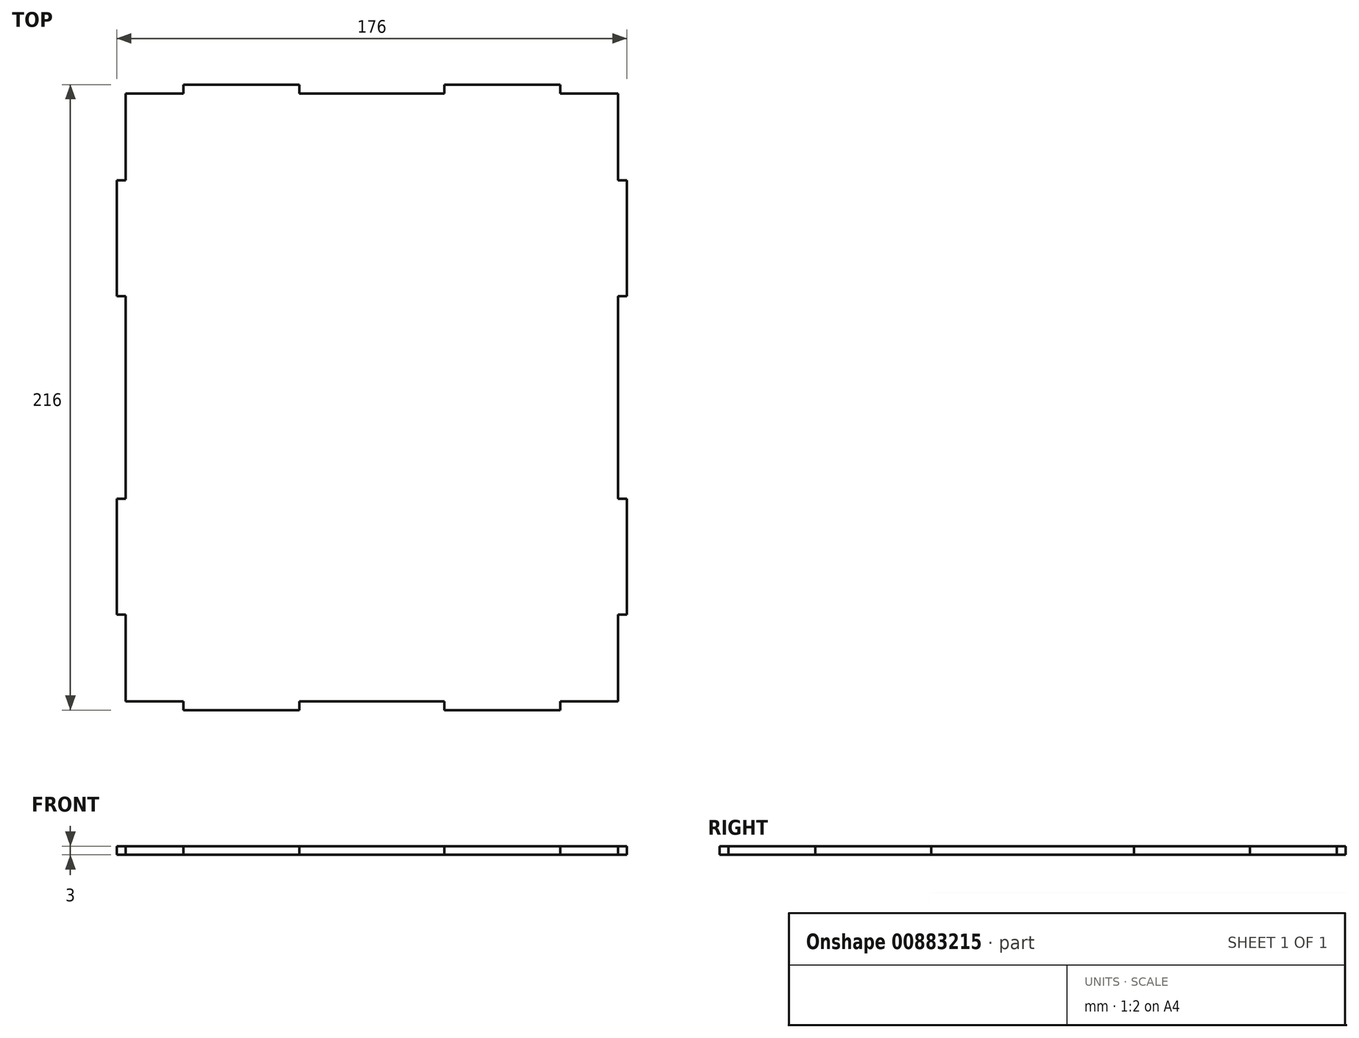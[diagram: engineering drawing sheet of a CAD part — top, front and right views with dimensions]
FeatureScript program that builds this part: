
annotation { "Feature Type Name" : "Feature", "Feature Type Description" : "" }
export const myFeature = defineFeature(function(context is Context, id is Id, definition is map)
    precondition{}
    {
        {
            var Q0;
            Q0=qCreatedBy(makeId("Top.planeOp"),FACE);
            var sketch = newSketch(context, id + "F0", { "sketchPlane" : qUnion([Q0])});
            skLineSegment(sketch, "E0.bottom", {"start": v(85, 105) * mm, "end": v(-85, 105) * mm});
            skLineSegment(sketch, "E0.top", {"start": v(85, -105) * mm, "end": v(-85, -105) * mm});
            skLineSegment(sketch, "E0.left", {"start": v(85, 105) * mm, "end": v(85, -105) * mm});
            skLineSegment(sketch, "E0.right", {"start": v(-85, 105) * mm, "end": v(-85, -105) * mm});
            skPoint(sketch, "E0.middle", {"position": v(0, 0) * mm});
            skLineSegment(sketch, "E1", {"start": v(85, 75) * mm, "end": v(88, 75) * mm});
            skLineSegment(sketch, "E2", {"start": v(88, 75) * mm, "end": v(88, 35) * mm});
            skLineSegment(sketch, "E3", {"start": v(88, 35) * mm, "end": v(85, 35) * mm});
            skLineSegment(sketch, "E4", {"start": v(25, 105) * mm, "end": v(25, 108) * mm});
            skLineSegment(sketch, "E5", {"start": v(25, 108) * mm, "end": v(65, 108) * mm});
            skLineSegment(sketch, "E6", {"start": v(65, 108) * mm, "end": v(65, 105) * mm});
            skLineSegment(sketch, "E7.MirrorCS", {"start": v(65, -108) * mm, "end": v(65, -105) * mm});
            skLineSegment(sketch, "E8.MirrorCS", {"start": v(25, -108) * mm, "end": v(65, -108) * mm});
            skLineSegment(sketch, "E9.MirrorCS", {"start": v(25, -105) * mm, "end": v(25, -108) * mm});
            skLineSegment(sketch, "E10.MirrorCS", {"start": v(-88, 35) * mm, "end": v(-85, 35) * mm});
            skLineSegment(sketch, "E11.MirrorCS", {"start": v(-85, 75) * mm, "end": v(-88, 75) * mm});
            skLineSegment(sketch, "E12.MirrorCS", {"start": v(-88, 75) * mm, "end": v(-88, 35) * mm});
            skLineSegment(sketch, "E13", {"start": v(85, -75) * mm, "end": v(88, -75) * mm});
            skLineSegment(sketch, "E14", {"start": v(88, -75) * mm, "end": v(88, -35) * mm});
            skLineSegment(sketch, "E15", {"start": v(88, -35) * mm, "end": v(85, -35) * mm});
            skLineSegment(sketch, "E16.MirrorCS", {"start": v(-88, -35) * mm, "end": v(-85, -35) * mm});
            skLineSegment(sketch, "E17.MirrorCS", {"start": v(-88, -75) * mm, "end": v(-88, -35) * mm});
            skLineSegment(sketch, "E18.MirrorCS", {"start": v(-85, -75) * mm, "end": v(-88, -75) * mm});
            skLineSegment(sketch, "E19.MirrorCS", {"start": v(-25, 105) * mm, "end": v(-25, 108) * mm});
            skLineSegment(sketch, "E20.MirrorCS", {"start": v(-25, 108) * mm, "end": v(-65, 108) * mm});
            skLineSegment(sketch, "E21.MirrorCS", {"start": v(-65, 108) * mm, "end": v(-65, 105) * mm});
            skLineSegment(sketch, "E22.MirrorCS", {"start": v(-25, -105) * mm, "end": v(-25, -108) * mm});
            skLineSegment(sketch, "E23.MirrorCS", {"start": v(-25, -108) * mm, "end": v(-65, -108) * mm});
            skLineSegment(sketch, "E24.MirrorCS", {"start": v(-65, -108) * mm, "end": v(-65, -105) * mm});
            skSolve(sketch);
        }
        {
            var Q0;
            Q0 = qSketchRegion(id + "F0", true);
            extrude(context, id + "F1", {"entities" : qUnion([Q0]), "depth" : 3 * mm, "offsetDistance" : 25 * mm});
        }
    });
